# Revit family: ALUMOGIPS
name_source: partatom
category: Осветительные приборы
units: mm (PartAtom-declared; Revit-internal decimal feet)

## family parameters
Всегда вертикально = Нет
Источник света = Да
На основе рабочей плоскости = Нет
Общий = Нет
При загрузке вырезать с полостями = Нет
Размер круглого соединителя = Использовать диаметр
Тип детали = Нормальный
Точка расчета площади = Да

## types (72) — shared parameters
ADSK_Единица измерения = шт.
ADSK_Завод-изготовитель = ЗАО «Центрстройсвет»
ADSK_Классификация нагрузок = Прочее
ADSK_Количество фаз = 1
ADSK_Количество фаз числовое = 1
ADSK_Коэффициент мощности = 0.92
ADSK_Напряжение = 230 В
ADSK_Ток = 0 А
URL = http://csvt.ru
Видимая форма излучения при визуализации = Да
Высота = 40 мм
Изготовитель = ЗАО «Центрстройсвет»
Материал стекла = RAL светящийся
Светофильтр = 16777215
Смещение цветовой температуры при затухании лампы = <Нет>
Угол наклона = 90.00°

## per-type parameters (varying)
| type | ADSK_Код изделия | ADSK_Масса | ADSK_Наименование | ADSK_Номинальная мощность | ADSK_Обозначение | ADSK_Полная мощность | Длина | Излучение по длине прямоугольника | Излучение по ширине прямоугольника | Материал светильника | Файл фотометрической сетки | Ширина |
| Alumogips-22/opal-sand 295x295 (IP54, 4000К, серый) | ЦБ000007755 | 1 | Встраиваемый светодиодный светильник Alumogips-22/opal-sand 295x295 (IP54, 4000К, серый) | 22 Вт | Alumogips-22/opal-sand 295x295 (IP54, 4000К, серый) | 24 В·А | 295 мм | 275 мм | 275 мм | RAL 9006 | Светильник ALUMOGIPS-22 OPAL-SAND-(295x295).IES | 295 мм |
| Alumogips-22/opal-sand 295x295 (IP40, 4000К, серый) | ЦБ000006716 | 1 | Встраиваемый светодиодный светильник Alumogips-22/opal-sand 295x295 (IP40, 4000К, серый) | 22 Вт | Alumogips-22/opal-sand 295x295 (IP40, 4000К, серый) | 24 В·А | 295 мм | 275 мм | 275 мм | RAL 9006 | Светильник ALUMOGIPS-22 OPAL-SAND-(295x295).IES | 295 мм |
| Alumogips-22/opal-sand 295x295 (IP54, 4000К, белый) | ЦБ000007753 | 1 | Встраиваемый светодиодный светильник Alumogips-22/opal-sand 295x295 (IP54, 4000К, белый) | 22 Вт | Alumogips-22/opal-sand 295x295 (IP54, 4000К, белый) | 24 В·А | 295 мм | 275 мм | 275 мм | RAL 9001 | Светильник ALUMOGIPS-22 OPAL-SAND-(295x295).IES | 295 мм |
| Alumogips-22/opal-sand 295x295 (IP40, 4000К, белый) | ЦБ000007351 | 1 | Встраиваемый светодиодный светильник Alumogips-22/opal-sand 295x295 (IP40, 4000К, белый) | 22 Вт | Alumogips-22/opal-sand 295x295 (IP40, 4000К, белый) | 24 В·А | 295 мм | 275 мм | 275 мм | RAL 9001 | Светильник ALUMOGIPS-22 OPAL-SAND-(295x295).IES | 295 мм |
| Alumogips-38/opal-sand 610х610 (IP54, 4000К, серый, грильято) c БАП на 3 часа | ЦБ000007825 | 2.4 | Встраиваемый светодиодный светильник Alumogips-38/opal-sand 610х610 (IP54, 4000К, серый, грильято) c БАП на 3 часа | 38 Вт | Alumogips-38/opal-sand 610х610 (IP54, 4000К, серый, грильято) | 41 В·А | 610 мм | 590 мм | 590 мм | RAL 9006 | Светильник ALUMOGIPS-38 OPAL-SAND-(610x610).IES | 610 мм |
| Alumogips-38/opal-sand 610х610 (IP54, 4000К, серый, грильято) c БАП на 1 час | ЦБ000007816 | 2.4 | Встраиваемый светодиодный светильник Alumogips-38/opal-sand 610х610 (IP54, 4000К, серый, грильято) c БАП на 1 час | 38 Вт | Alumogips-38/opal-sand 610х610 (IP54, 4000К, серый, грильято) | 41 В·А | 610 мм | 590 мм | 590 мм | RAL 9006 | Светильник ALUMOGIPS-38 OPAL-SAND-(610x610).IES | 610 мм |
| Alumogips-38/opal-sand 610х610 (IP54, 4000К, серый, грильято) | ЦБ000007807 | 2.4 | Встраиваемый светодиодный светильник Alumogips-38/opal-sand 610х610 (IP54, 4000К, серый, грильято) | 38 Вт | Alumogips-38/opal-sand 610х610 (IP54, 4000К, серый, грильято) | 41 В·А | 610 мм | 590 мм | 590 мм | RAL 9006 | Светильник ALUMOGIPS-38 OPAL-SAND-(610x610).IES | 610 мм |
| Alumogips-38/opal-sand 610х610 (IP54, 4000К, белый, грильято) c БАП на 3 часа | ЦБ000007823 | 2.4 | Встраиваемый светодиодный светильник Alumogips-38/opal-sand 610х610 (IP54, 4000К, белый, грильято) c БАП на 3 часа | 38 Вт | Alumogips-38/opal-sand 610х610 (IP54, 4000К, белый, грильято) | 41 В·А | 610 мм | 590 мм | 590 мм | RAL 9001 | Светильник ALUMOGIPS-38 OPAL-SAND-(610x610).IES | 610 мм |
| Alumogips-38/opal-sand 610х610 (IP54, 4000К, белый, грильято) c БАП на 1 час | ЦБ000007814 | 2.4 | Встраиваемый светодиодный светильник Alumogips-38/opal-sand 610х610 (IP54, 4000К, белый, грильято) c БАП на 1 час | 38 Вт | Alumogips-38/opal-sand 610х610 (IP54, 4000К, белый, грильято) | 41 В·А | 610 мм | 590 мм | 590 мм | RAL 9001 | Светильник ALUMOGIPS-38 OPAL-SAND-(610x610).IES | 610 мм |
| Alumogips-38/opal-sand 610х610 (IP54, 4000К, белый, грильято) | ЦБ000007805 | 2.4 | Встраиваемый светодиодный светильник Alumogips-38/opal-sand 610х610 (IP54, 4000К, белый, грильято) | 38 Вт | Alumogips-38/opal-sand 610х610 (IP54, 4000К, белый, грильято) | 41 В·А | 610 мм | 590 мм | 590 мм | RAL 9001 | Светильник ALUMOGIPS-38 OPAL-SAND-(610x610).IES | 610 мм |
| Alumogips-38/opal-sand 610х610 (IP40, 4000К, серый, грильято) c БАП на 3 часа | ЦБ000007821 | 2.4 | Встраиваемый светодиодный светильник Alumogips-38/opal-sand 610х610 (IP40, 4000К, серый, грильято) c БАП на 3 часа | 38 Вт | Alumogips-38/opal-sand 610х610 (IP40, 4000К, серый, грильято) | 41 В·А | 610 мм | 590 мм | 590 мм | RAL 9006 | Светильник ALUMOGIPS-38 OPAL-SAND-(610x610).IES | 610 мм |
| Alumogips-38/opal-sand 610х610 (IP40, 4000К, серый, грильято) c БАП на 1 час | ЦБ000007812 | 2.4 | Встраиваемый светодиодный светильник Alumogips-38/opal-sand 610х610 (IP40, 4000К, серый, грильято) c БАП на 1 час | 38 Вт | Alumogips-38/opal-sand 610х610 (IP40, 4000К, серый, грильято) | 41 В·А | 610 мм | 590 мм | 590 мм | RAL 9006 | Светильник ALUMOGIPS-38 OPAL-SAND-(610x610).IES | 610 мм |
| Alumogips-38/opal-sand 610х610 (IP40, 4000К, серый, грильято) | ЦБ000007803 | 2.4 | Встраиваемый светодиодный светильник Alumogips-38/opal-sand 610х610 (IP40, 4000К, серый, грильято) | 38 Вт | Alumogips-38/opal-sand 610х610 (IP40, 4000К, серый, грильято) | 41 В·А | 610 мм | 590 мм | 590 мм | RAL 9006 | Светильник ALUMOGIPS-38 OPAL-SAND-(610x610).IES | 610 мм |
| Alumogips-38/opal-sand 610х610 (IP40, 4000К, белый, грильято) c БАП на 3 часа | ЦБ000007819 | 2.4 | Встраиваемый светодиодный светильник Alumogips-38/opal-sand 610х610 (IP40, 4000К, белый, грильято) c БАП на 3 часа | 38 Вт | Alumogips-38/opal-sand 610х610 (IP40, 4000К, белый, грильято) | 41 В·А | 610 мм | 590 мм | 590 мм | RAL 9001 | Светильник ALUMOGIPS-38 OPAL-SAND-(610x610).IES | 610 мм |
| Alumogips-38/opal-sand 610х610 (IP40, 4000К, белый, грильято) c БАП на 1 час | ЦБ000007809 | 2.4 | Встраиваемый светодиодный светильник Alumogips-38/opal-sand 610х610 (IP40, 4000К, белый, грильято) c БАП на 1 час | 38 Вт | Alumogips-38/opal-sand 610х610 (IP40, 4000К, белый, грильято) | 41 В·А | 610 мм | 590 мм | 590 мм | RAL 9001 | Светильник ALUMOGIPS-38 OPAL-SAND-(610x610).IES | 610 мм |
| Alumogips-38/opal-sand 610х610 (IP40, 4000К, белый, грильято) | ЦБ000007801 | 2.4 | Встраиваемый светодиодный светильник Alumogips-38/opal-sand 610х610 (IP40, 4000К, белый, грильято) | 38 Вт | Alumogips-38/opal-sand 610х610 (IP40, 4000К, белый, грильято) | 41 В·А | 610 мм | 590 мм | 590 мм | RAL 9001 | Светильник ALUMOGIPS-38 OPAL-SAND-(610x610).IES | 610 мм |
| Alumogips-50/opal-sand 610х610 (IP54, 4000К, серый, грильято) | ЦБ000007837 | 2.5 | Встраиваемый светодиодный светильник Alumogips-50/opal-sand 610х610 (IP54, 4000К, серый, грильято) | 50 Вт | Alumogips-50/opal-sand 610х610 (IP54, 4000К, серый, грильято) | 54 В·А | 610 мм | 590 мм | 590 мм | RAL 9006 | Светильник ALUMOGIPS-50 OPAL-SAND-(610x610).IES | 610 мм |
| Alumogips-50/opal-sand 610х610 (IP54, 4000К, белый, грильято) | ЦБ000007835 | 2.5 | Встраиваемый светодиодный светильник Alumogips-50/opal-sand 610х610 (IP54, 4000К, белый, грильято) | 50 Вт | Alumogips-50/opal-sand 610х610 (IP54, 4000К, белый, грильято) | 54 В·А | 610 мм | 590 мм | 590 мм | RAL 9001 | Светильник ALUMOGIPS-50 OPAL-SAND-(610x610).IES | 610 мм |
| Alumogips-50/opal-sand 610х610 (IP40, 4000К, серый, грильято) | ЦБ000007831 | 2.5 | Встраиваемый светодиодный светильник Alumogips-50/opal-sand 610х610 (IP40, 4000К, серый, грильято) | 50 Вт | Alumogips-50/opal-sand 610х610 (IP40, 4000К, серый, грильято) | 54 В·А | 610 мм | 590 мм | 590 мм | RAL 9006 | Светильник ALUMOGIPS-50 OPAL-SAND-(610x610).IES | 610 мм |
| Alumogips-50/opal-sand 610х610 (IP40, 4000К, белый, грильято) | ЦБ000007833 | 2.5 | Встраиваемый светодиодный светильник Alumogips-50/opal-sand 610х610 (IP40, 4000К, белый, грильято) | 50 Вт | Alumogips-50/opal-sand 610х610 (IP40, 4000К, белый, грильято) | 54 В·А | 610 мм | 590 мм | 590 мм | RAL 9001 | Светильник ALUMOGIPS-50 OPAL-SAND-(610x610).IES | 610 мм |
| Alumogips-76/opal-sand 595х1195 (IP54, 4000К, серый) | ЦБ000008056 | 5 | Встраиваемый светодиодный светильник Alumogips-76/opal-sand 595х1195 (IP54, 4000К, серый) | 76 Вт | Alumogips-76/opal-sand 595х1195 (IP54, 4000К, серый) | 83 В·А | 1195 мм | 1175 мм | 575 мм | RAL 9006 | Светильник ALUMOGIPS-76 OPAL-SAND-(595x1195).IES | 595 мм |
| Alumogips-76/opal-sand 595х1195 (IP54, 4000К, белый) | ЦБ000008051 | 5 | Встраиваемый светодиодный светильник Alumogips-76/opal-sand 595х1195 (IP54, 4000К, белый) | 76 Вт | Alumogips-76/opal-sand 595х1195 (IP54, 4000К, белый) | 83 В·А | 1195 мм | 1175 мм | 575 мм | RAL 9001 | Светильник ALUMOGIPS-76 OPAL-SAND-(595x1195).IES | 595 мм |
| Alumogips-76/opal-sand 595х1195 (IP40, 4000К, серый) | ЦБ000007032 | 5 | Встраиваемый светодиодный светильник Alumogips-76/opal-sand 595х1195 (IP40, 4000К, серый) | 76 Вт | Alumogips-76/opal-sand 595х1195 (IP40, 4000К, серый) | 83 В·А | 1195 мм | 1175 мм | 575 мм | RAL 9006 | Светильник ALUMOGIPS-76 OPAL-SAND-(595x1195).IES | 595 мм |
| Alumogips-76/opal-sand 595х1195 (IP40, 4000К, белый) | ЦБ000007359 | 5 | Встраиваемый светодиодный светильник Alumogips-76/opal-sand 595х1195 (IP40, 4000К, белый) | 76 Вт | Alumogips-76/opal-sand 595х1195 (IP40, 4000К, белый) | 83 В·А | 1195 мм | 1175 мм | 575 мм | RAL 9001 | Светильник ALUMOGIPS-76 OPAL-SAND-(595x1195).IES | 595 мм |
| Alumogips-76/opal-sand 295х1195 (IP54, 4000К, серый) | ЦБ000007971 | 2.5 | Встраиваемый светодиодный светильник Alumogips-76/opal-sand 295х1195 (IP54, 4000К, серый) | 76 Вт | Alumogips-76/opal-sand 295х1195 (IP54, 4000К, серый) | 83 В·А | 1195 мм | 1175 мм | 275 мм | RAL 9006 | Светильник ALUMOGIPS-76 OPAL-SAND-(295x1195).ies | 295 мм |
| Alumogips-76/opal-sand 295х1195 (IP54, 4000К, белый) | ЦБ000007969 | 2.5 | Встраиваемый светодиодный светильник Alumogips-76/opal-sand 295х1195 (IP54, 4000К, белый) | 76 Вт | Alumogips-76/opal-sand 295х1195 (IP54, 4000К, белый) | 83 В·А | 1195 мм | 1175 мм | 275 мм | RAL 9001 | Светильник ALUMOGIPS-76 OPAL-SAND-(295x1195).ies | 295 мм |
| Alumogips-76/opal-sand 295х1195 (IP40, 4000К, серый) | ЦБ000007942 | 2.5 | Встраиваемый светодиодный светильник Alumogips-76/opal-sand 295х1195 (IP40, 4000К, серый) | 76 Вт | Alumogips-76/opal-sand 295х1195 (IP40, 4000К, серый) | 83 В·А | 1195 мм | 1175 мм | 275 мм | RAL 9006 | Светильник ALUMOGIPS-76 OPAL-SAND-(295x1195).ies | 295 мм |
| Alumogips-76/opal-sand 295х1195 (IP40, 4000К, белый) | ЦБ000007455 | 2.5 | Встраиваемый светодиодный светильник Alumogips-76/opal-sand 295х1195 (IP40, 4000К, белый) | 76 Вт | Alumogips-76/opal-sand 295х1195 (IP40, 4000К, белый) | 83 В·А | 1195 мм | 1175 мм | 275 мм | RAL 9001 | Светильник ALUMOGIPS-76 OPAL-SAND-(295x1195).ies | 295 мм |
| Alumogips-76/opal-sand 160х2305 (IP54, 4000К, серый) | ЦБ000008090 | 3 | Встраиваемый светодиодный светильник Alumogips-76/opal-sand 160х2305 (IP54, 4000К, серый) | 76 Вт | Alumogips-76/opal-sand 160х2305 (IP54, 4000К, серый) | 83 В·А | 2305 мм | 2285 мм | 140 мм | RAL 9006 | Светильник ALUMOGIPS-76 OPAL-SAND-(160x2300).IES | 160 мм |
| Alumogips-76/opal-sand 160х2305 (IP54, 4000К, белый) | ЦБ000008088 | 3 | Встраиваемый светодиодный светильник Alumogips-76/opal-sand 160х2305 (IP54, 4000К, белый) | 76 Вт | Alumogips-76/opal-sand 160х2305 (IP54, 4000К, белый) | 83 В·А | 2305 мм | 2285 мм | 140 мм | RAL 9001 | Светильник ALUMOGIPS-76 OPAL-SAND-(160x2300).IES | 160 мм |
| Alumogips-76/opal-sand 160х2305 (IP40, 4000К, серый) | ЦБ000008086 | 3 | Встраиваемый светодиодный светильник Alumogips-76/opal-sand 160х2305 (IP40, 4000К, серый) | 76 Вт | Alumogips-76/opal-sand 160х2305 (IP40, 4000К, серый) | 83 В·А | 2305 мм | 2285 мм | 140 мм | RAL 9006 | Светильник ALUMOGIPS-76 OPAL-SAND-(160x2300).IES | 160 мм |
| Alumogips-76/opal-sand 160х2305 (IP40, 4000К, белый) | ЦБ000008084 | 3 | Встраиваемый светодиодный светильник Alumogips-76/opal-sand 160х2305 (IP40, 4000К, белый) | 76 Вт | Alumogips-76/opal-sand 160х2305 (IP40, 4000К, белый) | 83 В·А | 2305 мм | 2285 мм | 140 мм | RAL 9001 | Светильник ALUMOGIPS-76 OPAL-SAND-(160x2300).IES | 160 мм |
| Alumogips-50/opal-sand 595х595 (IP54, 4000К, серый) | ЦБ000006734 | 2.5 | Встраиваемый светодиодный светильник Alumogips-50/opal-sand 595х595 (IP54, 4000К, серый) | 50 Вт | Alumogips-50/opal-sand 595х595 (IP54, 4000К, серый) | 54 В·А | 595 мм | 575 мм | 575 мм | RAL 9006 | Светильник ALUMOGIPS-50 OPAL-SAND-(595x595).IES | 595 мм |
| Alumogips-50/opal-sand 595х595 (IP54, 4000К, белый) | ЦБ000007362 | 2.5 | Встраиваемый светодиодный светильник Alumogips-50/opal-sand 595х595 (IP54, 4000К, белый) | 50 Вт | Alumogips-50/opal-sand 595х595 (IP54, 4000К, белый) | 54 В·А | 595 мм | 575 мм | 575 мм | RAL 9001 | Светильник ALUMOGIPS-50 OPAL-SAND-(595x595).IES | 595 мм |
| Alumogips-50/opal-sand 595х595 (IP40, 4000К, серый) | ЦБ000006727 | 2.5 | Встраиваемый светодиодный светильник Alumogips-50/opal-sand 595х595 (IP40, 4000К, серый) | 50 Вт | Alumogips-50/opal-sand 595х595 (IP40, 4000К, серый) | 54 В·А | 595 мм | 575 мм | 575 мм | RAL 9006 | Светильник ALUMOGIPS-50 OPAL-SAND-(595x595).IES | 595 мм |
| Alumogips-50/opal-sand 595х595 (IP40, 4000К, белый) | ЦБ000007340 | 2.5 | Встраиваемый светодиодный светильник Alumogips-50/opal-sand 595х595 (IP40, 4000К, белый) | 50 Вт | Alumogips-50/opal-sand 595х595 (IP40, 4000К, белый) | 54 В·А | 595 мм | 575 мм | 575 мм | RAL 9001 | Светильник ALUMOGIPS-50 OPAL-SAND-(595x595).IES | 595 мм |
| Alumogips-38/opal-sand 595х595 (IP54, 4000К, серый) c БАП на 3 часа | ЦБ000008033 | 2.4 | Встраиваемый светодиодный светильник Alumogips-38/opal-sand 595х595 (IP54, 4000К, серый) c БАП на 3 час | 38 Вт | Alumogips-38/opal-sand 595х595 (IP54, 4000К, серый) | 41 В·А | 595 мм | 575 мм | 575 мм | RAL 9006 | Светильник ALUMOGIPS-38 OPAL-SAND-(595x595).IES | 595 мм |
| Alumogips-38/opal-sand 595х595 (IP54, 4000К, серый) c БАП на 1 час | ЦБ000007256 | 2.4 | Встраиваемый светодиодный светильник Alumogips-38/opal-sand 595х595 (IP54, 4000К, серый) c БАП на 1 час | 38 Вт | Alumogips-38/opal-sand 595х595 (IP54, 4000К, серый) | 41 В·А | 595 мм | 575 мм | 575 мм | RAL 9006 | Светильник ALUMOGIPS-38 OPAL-SAND-(595x595).IES | 595 мм |
| Alumogips-38/opal-sand 595х595 (IP54, 4000К, серый) | ЦБ000006732 | 2.4 | Встраиваемый светодиодный светильник Alumogips-38/opal-sand 595х595 (IP54, 4000К, серый) | 38 Вт | Alumogips-38/opal-sand 595х595 (IP54, 4000К, серый) | 41 В·А | 595 мм | 575 мм | 575 мм | RAL 9006 | Светильник ALUMOGIPS-38 OPAL-SAND-(595x595).IES | 595 мм |
| Alumogips-38/opal-sand 595х595 (IP54, 4000К, белый) c БАП на 3 часа | ЦБ000008031 | 2.4 | Встраиваемый светодиодный светильник Alumogips-38/opal-sand 595х595 (IP54, 4000К, белый) c БАП на 3 час | 38 Вт | Alumogips-38/opal-sand 595х595 (IP54, 4000К, белый) | 41 В·А | 595 мм | 575 мм | 575 мм | RAL 9001 | Светильник ALUMOGIPS-38 OPAL-SAND-(595x595).IES | 595 мм |
| Alumogips-38/opal-sand 595х595 (IP54, 4000К, белый) c БАП на 1 час | ЦБ000007446 | 2.4 | Встраиваемый светодиодный светильник Alumogips-38/opal-sand 595х595 (IP54, 4000К, белый) c БАП на 1 час | 38 Вт | Alumogips-38/opal-sand 595х595 (IP54, 4000К, белый) | 41 В·А | 595 мм | 575 мм | 575 мм | RAL 9001 | Светильник ALUMOGIPS-38 OPAL-SAND-(595x595).IES | 595 мм |
| Alumogips-38/opal-sand 595х595 (IP54, 4000К, белый) | ЦБ000007360 | 2.4 | Встраиваемый светодиодный светильник Alumogips-38/opal-sand 595х595 (IP54, 4000К, белый) | 38 Вт | Alumogips-38/opal-sand 595х595 (IP54, 4000К, белый) | 41 В·А | 595 мм | 575 мм | 575 мм | RAL 9001 | Светильник ALUMOGIPS-38 OPAL-SAND-(595x595).IES | 595 мм |
| Alumogips-38/opal-sand 595х595 (IP40, 4000К, серый) c БАП на 3 часа | ЦБ000008029 | 2.4 | Встраиваемый светодиодный светильник Alumogips-38/opal-sand 595х595 (IP40, 4000К, серый) c БАП на 3 час | 38 Вт | Alumogips-38/opal-sand 595х595 (IP40, 4000К, серый) | 41 В·А | 595 мм | 575 мм | 575 мм | RAL 9006 | Светильник ALUMOGIPS-38 OPAL-SAND-(595x595).IES | 595 мм |
| Alumogips-38/opal-sand 595х595 (IP40, 4000К, серый) c БАП на 1 час | ЦБ000007062 | 2.4 | Встраиваемый светодиодный светильник Alumogips-38/opal-sand 595х595 (IP40, 4000К, серый) c БАП на 1 час | 38 Вт | Alumogips-38/opal-sand 595х595 (IP40, 4000К, серый) | 41 В·А | 595 мм | 575 мм | 575 мм | RAL 9006 | Светильник ALUMOGIPS-38 OPAL-SAND-(595x595).IES | 595 мм |
| Alumogips-38/opal-sand 595х595 (IP40, 4000К, серый) | ЦБ000006722 | 2.4 | Встраиваемый светодиодный светильник Alumogips-38/opal-sand 595х595 (IP40, 4000К, серый) | 38 Вт | Alumogips-38/opal-sand 595х595 (IP40, 4000К, серый) | 41 В·А | 595 мм | 575 мм | 575 мм | RAL 9006 | Светильник ALUMOGIPS-38 OPAL-SAND-(595x595).IES | 595 мм |
| Alumogips-38/opal-sand 595х595 (IP40, 4000К, белый) c БАП на 3 часа | ЦБ000008027 | 2.4 | Встраиваемый светодиодный светильник Alumogips-38/opal-sand 595х595 (IP40, 4000К, белый) c БАП на 3 час | 38 Вт | Alumogips-38/opal-sand 595х595 (IP40, 4000К, белый) | 41 В·А | 595 мм | 575 мм | 575 мм | RAL 9001 | Светильник ALUMOGIPS-38 OPAL-SAND-(595x595).IES | 595 мм |
| Alumogips-38/opal-sand 595х595 (IP40, 4000К, белый) c БАП на 1 час | ЦБ000008022 | 2.4 | Встраиваемый светодиодный светильник Alumogips-38/opal-sand 595х595 (IP40, 4000К, белый) c БАП на 1 час | 38 Вт | Alumogips-38/opal-sand 595х595 (IP40, 4000К, белый) | 41 В·А | 595 мм | 575 мм | 575 мм | RAL 9001 | Светильник ALUMOGIPS-38 OPAL-SAND-(595x595).IES | 595 мм |
| Alumogips-38/opal-sand 595х595 (IP40, 4000К, белый) | ЦБ000007355 | 2.4 | Встраиваемый светодиодный светильник Alumogips-38/opal-sand 595х595 (IP40, 4000К, белый) | 38 Вт | Alumogips-38/opal-sand 595х595 (IP40, 4000К, белый) | 41 В·А | 595 мм | 575 мм | 575 мм | RAL 9001 | Светильник ALUMOGIPS-38 OPAL-SAND-(595x595).IES | 595 мм |
| Alumogips-38/opal-sand 295х1195 (IP54, 4000К, серый) c БАП на 3 часа | ЦБ000008016 | 2.5 | Встраиваемый светодиодный светильник Alumogips-38/opal-sand 295х1195 (IP54, 4000К, серый) c БАП на 3 час | 38 Вт | Alumogips-38/opal-sand 295х1195 (IP54, 4000К, серый) | 41 В·А | 1195 мм | 1175 мм | 275 мм | RAL 9006 | Светильник ALUMOGIPS-38 OPAL-SAND-(295x1195).ies | 295 мм |
| Alumogips-38/opal-sand 295х1195 (IP54, 4000К, серый) c БАП на 1 час | ЦБ000008604 | 2.5 | Встраиваемый светодиодный светильник Alumogips-38/opal-sand 295х1195 (IP54, 4000К, серый) c БАП на 1 час | 38 Вт | Alumogips-38/opal-sand 295х1195 (IP54, 4000К, серый) | 41 В·А | 1195 мм | 1175 мм | 275 мм | RAL 9006 | Светильник ALUMOGIPS-38 OPAL-SAND-(295x1195).ies | 295 мм |
| Alumogips-38/opal-sand 295х1195 (IP54, 4000К, серый) | ЦБ000007946 | 2.5 | Встраиваемый светодиодный светильник Alumogips-38/opal-sand 295х1195 (IP54, 4000К, серый) | 38 Вт | Alumogips-38/opal-sand 295х1195 (IP54, 4000К, серый) | 41 В·А | 1195 мм | 1175 мм | 275 мм | RAL 9006 | Светильник ALUMOGIPS-38 OPAL-SAND-(295x1195).ies | 295 мм |
| Alumogips-38/opal-sand 295х1195 (IP54, 4000К, белый) с БАП на 3 часа | ЦБ000008606 | 2.5 | Встраиваемый светодиодный светильник Alumogips-38/opal-sand 295х1195 (IP54, 4000К, белый) с БАП на 3 часа | 38 Вт | Alumogips-38/opal-sand 295х1195 (IP54, 4000К, белый) | 41 В·А | 1195 мм | 1175 мм | 275 мм | RAL 9001 | Светильник ALUMOGIPS-38 OPAL-SAND-(295x1195).ies | 295 мм |
| Alumogips-38/opal-sand 295х1195 (IP54, 4000К, белый) c БАП на 1 час | ЦБ000008014 | 2.5 | Встраиваемый светодиодный светильник Alumogips-38/opal-sand 295х1195 (IP54, 4000К, белый) c БАП на 1 час | 38 Вт | Alumogips-38/opal-sand 295х1195 (IP54, 4000К, белый) | 41 В·А | 1195 мм | 1175 мм | 275 мм | RAL 9001 | Светильник ALUMOGIPS-38 OPAL-SAND-(295x1195).ies | 295 мм |
| Alumogips-38/opal-sand 295х1195 (IP54, 4000К, белый) | ЦБ000007944 | 2.5 | Встраиваемый светодиодный светильник Alumogips-38/opal-sand 295х1195 (IP54, 4000К, белый) | 38 Вт | Alumogips-38/opal-sand 295х1195 (IP54, 4000К, белый) | 41 В·А | 1195 мм | 1175 мм | 275 мм | RAL 9001 | Светильник ALUMOGIPS-38 OPAL-SAND-(295x1195).ies | 295 мм |
| Alumogips-38/opal-sand 295х1195 (IP40, 4000К, серый) c БАП на 3 часа | ЦБ000007976 | 2.5 | Встраиваемый светодиодный светильник Alumogips-38/opal-sand 295х1195 (IP40, 4000К, серый) c БАП на 3 час | 38 Вт | Alumogips-38/opal-sand 295х1195 (IP40, 4000К, серый) | 41 В·А | 1195 мм | 1175 мм | 275 мм | RAL 9006 | Светильник ALUMOGIPS-38 OPAL-SAND-(295x1195).ies | 295 мм |
| Alumogips-38/opal-sand 295х1195 (IP40, 4000К, серый) c БАП на 1 час | ЦБ000008600 | 2.5 | Встраиваемый светодиодный светильник Alumogips-38/opal-sand 295х1195 (IP40, 4000К, серый) c БАП на 1 час | 38 Вт | Alumogips-38/opal-sand 295х1195 (IP40, 4000К, серый) | 41 В·А | 1195 мм | 1175 мм | 275 мм | RAL 9006 | Светильник ALUMOGIPS-38 OPAL-SAND-(295x1195).ies | 295 мм |
| Alumogips-38/opal-sand 295х1195 (IP40, 4000К, серый) | ЦБ000007184 | 2.5 | Встраиваемый светодиодный светильник Alumogips-38/opal-sand 295х1195 (IP40, 4000К, серый) | 38 Вт | Alumogips-38/opal-sand 295х1195 (IP40, 4000К, серый) | 41 В·А | 1195 мм | 1175 мм | 275 мм | RAL 9006 | Светильник ALUMOGIPS-38 OPAL-SAND-(295x1195).ies | 295 мм |
| Alumogips-38/opal-sand 295х1195 (IP40, 4000К, белый) с БАП на 3 часа | ЦБ000007975 | 2.5 | Встраиваемый светодиодный светильник Alumogips-38/opal-sand 295х1195 (IP40, 4000К, белый) с БАП на 3 часа | 38 Вт | Alumogips-38/opal-sand 295х1195 (IP40, 4000К, белый) | 41 В·А | 1195 мм | 1175 мм | 275 мм | RAL 9001 | Светильник ALUMOGIPS-38 OPAL-SAND-(295x1195).ies | 295 мм |
| Alumogips-38/opal-sand 295х1195 (IP40, 4000К, белый) c БАП на 1 час | ЦБ000007973 | 2.5 | Встраиваемый светодиодный светильник Alumogips-38/opal-sand 295х1195 (IP40, 4000К, белый) c БАП на 1 час | 38 Вт | Alumogips-38/opal-sand 295х1195 (IP40, 4000К, белый) | 41 В·А | 1195 мм | 1175 мм | 275 мм | RAL 9001 | Светильник ALUMOGIPS-38 OPAL-SAND-(295x1195).ies | 295 мм |
| Alumogips-38/opal-sand 295х1195 (IP40, 4000К, белый) | ЦБ000007453 | 2.5 | Встраиваемый светодиодный светильник Alumogips-38/opal-sand 295х1195 (IP40, 4000К, белый) | 38 Вт | Alumogips-38/opal-sand 295х1195 (IP40, 4000К, белый) | 41 В·А | 1195 мм | 1175 мм | 275 мм | RAL 9001 | Светильник ALUMOGIPS-38 OPAL-SAND-(295x1195).ies | 295 мм |
| Alumogips-30/opal-sand 295х595 (IP54, 4000К, серый) c БАП на 3 часа | ЦБ000007781 | 1.3 | Встраиваемый светодиодный светильник Alumogips-30/opal-sand 295х595 (IP54, 4000К, серый) c БАП на 3 час | 30 Вт | Alumogips-30/opal-sand 295х595 (IP54, 4000К, серый) | 33 В·А | 595 мм | 575 мм | 275 мм | RAL 9006 | Светильник ALUMOGIPS-30 OPAL-SAND-(295x595).IES | 295 мм |
| Alumogips-30/opal-sand 295х595 (IP54, 4000К, серый) c БАП на 1 час | ЦБ000007773 | 1.3 | Встраиваемый светодиодный светильник Alumogips-30/opal-sand 295х595 (IP54, 4000К, серый) c БАП на 1 час | 30 Вт | Alumogips-30/opal-sand 295х595 (IP54, 4000К, серый) | 33 В·А | 595 мм | 575 мм | 275 мм | RAL 9006 | Светильник ALUMOGIPS-30 OPAL-SAND-(295x595).IES | 295 мм |
| Alumogips-30/opal-sand 295х595 (IP54, 4000К, серый) | ЦБ000007764 | 1.3 | Встраиваемый светодиодный светильник Alumogips-30/opal-sand 295х595 (IP54, 4000К, серый) | 30 Вт | Alumogips-30/opal-sand 295х595 (IP54, 4000К, серый) | 33 В·А | 595 мм | 575 мм | 275 мм | RAL 9006 | Светильник ALUMOGIPS-30 OPAL-SAND-(295x595).IES | 295 мм |
| Alumogips-30/opal-sand 295х595 (IP54, 4000К, белый) c БАП на 3 часа | ЦБ000007779 | 1.3 | Встраиваемый светодиодный светильник Alumogips-30/opal-sand 295х595 (IP54, 4000К, белый) c БАП на 3 час | 30 Вт | Alumogips-30/opal-sand 295х595 (IP54, 4000К, белый) | 33 В·А | 595 мм | 575 мм | 275 мм | RAL 9001 | Светильник ALUMOGIPS-30 OPAL-SAND-(295x595).IES | 295 мм |
| Alumogips-30/opal-sand 295х595 (IP54, 4000К, белый) c БАП на 1 час | ЦБ000007771 | 1.3 | Встраиваемый светодиодный светильник Alumogips-30/opal-sand 295х595 (IP54, 4000К, белый) c БАП на 1 час | 30 Вт | Alumogips-30/opal-sand 295х595 (IP54, 4000К, белый) | 33 В·А | 595 мм | 575 мм | 275 мм | RAL 9001 | Светильник ALUMOGIPS-30 OPAL-SAND-(295x595).IES | 295 мм |
| Alumogips-30/opal-sand 295х595 (IP54, 4000К, белый) | ЦБ000007762 | 1.3 | Встраиваемый светодиодный светильник Alumogips-30/opal-sand 295х595 (IP54, 4000К, белый) | 30 Вт | Alumogips-30/opal-sand 295х595 (IP54, 4000К, белый) | 33 В·А | 595 мм | 575 мм | 275 мм | RAL 9001 | Светильник ALUMOGIPS-30 OPAL-SAND-(295x595).IES | 295 мм |
| Alumogips-30/opal-sand 295х595 (IP40, 4000К, серый) c БАП на 3 часа | ЦБ000007777 | 1.3 | Встраиваемый светодиодный светильник Alumogips-30/opal-sand 295х595 (IP40, 4000К, серый) c БАП на 3 час | 30 Вт | Alumogips-30/opal-sand 295х595 (IP40, 4000К, серый) | 33 В·А | 595 мм | 575 мм | 275 мм | RAL 9006 | Светильник ALUMOGIPS-30 OPAL-SAND-(295x595).IES | 295 мм |
| Alumogips-30/opal-sand 295х595 (IP40, 4000К, серый) c БАП на 1 час | ЦБ000007158 | 1.3 | Встраиваемый светодиодный светильник Alumogips-30/opal-sand 295х595 (IP40, 4000К, серый) c БАП на 1 час | 30 Вт | Alumogips-30/opal-sand 295х595 (IP40, 4000К, серый) | 33 В·А | 595 мм | 575 мм | 275 мм | RAL 9006 | Светильник ALUMOGIPS-30 OPAL-SAND-(295x595).IES | 295 мм |
| Alumogips-30/opal-sand 295х595 (IP40, 4000К, серый) | ЦБ000006719 | 1.3 | Встраиваемый светодиодный светильник Alumogips-30/opal-sand 295х595 (IP40, 4000К, серый) | 30 Вт | Alumogips-30/opal-sand 295х595 (IP40, 4000К, серый) | 33 В·А | 595 мм | 575 мм | 275 мм | RAL 9006 | Светильник ALUMOGIPS-30 OPAL-SAND-(295x595).IES | 295 мм |
| Alumogips-30/opal-sand 295х595 (IP40, 4000К, белый) c БАП на 3 часа | ЦБ000007775 | 1.3 | Встраиваемый светодиодный светильник Alumogips-30/opal-sand 295х595 (IP40, 4000К, белый) c БАП на 3 час | 30 Вт | Alumogips-30/opal-sand 295х595 (IP40, 4000К, белый) | 33 В·А | 595 мм | 575 мм | 275 мм | RAL 9001 | Светильник ALUMOGIPS-30 OPAL-SAND-(295x595).IES | 295 мм |
| Alumogips-30/opal-sand 295х595 (IP40, 4000К, белый) c БАП на 1 час | ЦБ000007768 | 1.3 | Встраиваемый светодиодный светильник Alumogips-30/opal-sand 295х595 (IP40, 4000К, белый) c БАП на 1 час | 30 Вт | Alumogips-30/opal-sand 295х595 (IP40, 4000К, белый) | 33 В·А | 595 мм | 575 мм | 275 мм | RAL 9001 | Светильник ALUMOGIPS-30 OPAL-SAND-(295x595).IES | 295 мм |
| Alumogips-30/opal-sand 295х595 (IP40, 4000К, белый) | ЦБ000007353 | 1.3 | Встраиваемый светодиодный светильник Alumogips-30/opal-sand 295х595 (IP40, 4000К, белый) | 30 Вт | Alumogips-30/opal-sand 295х595 (IP40, 4000К, белый) | 33 В·А | 595 мм | 575 мм | 275 мм | RAL 9001 | Светильник ALUMOGIPS-30 OPAL-SAND-(295x595).IES | 295 мм |
